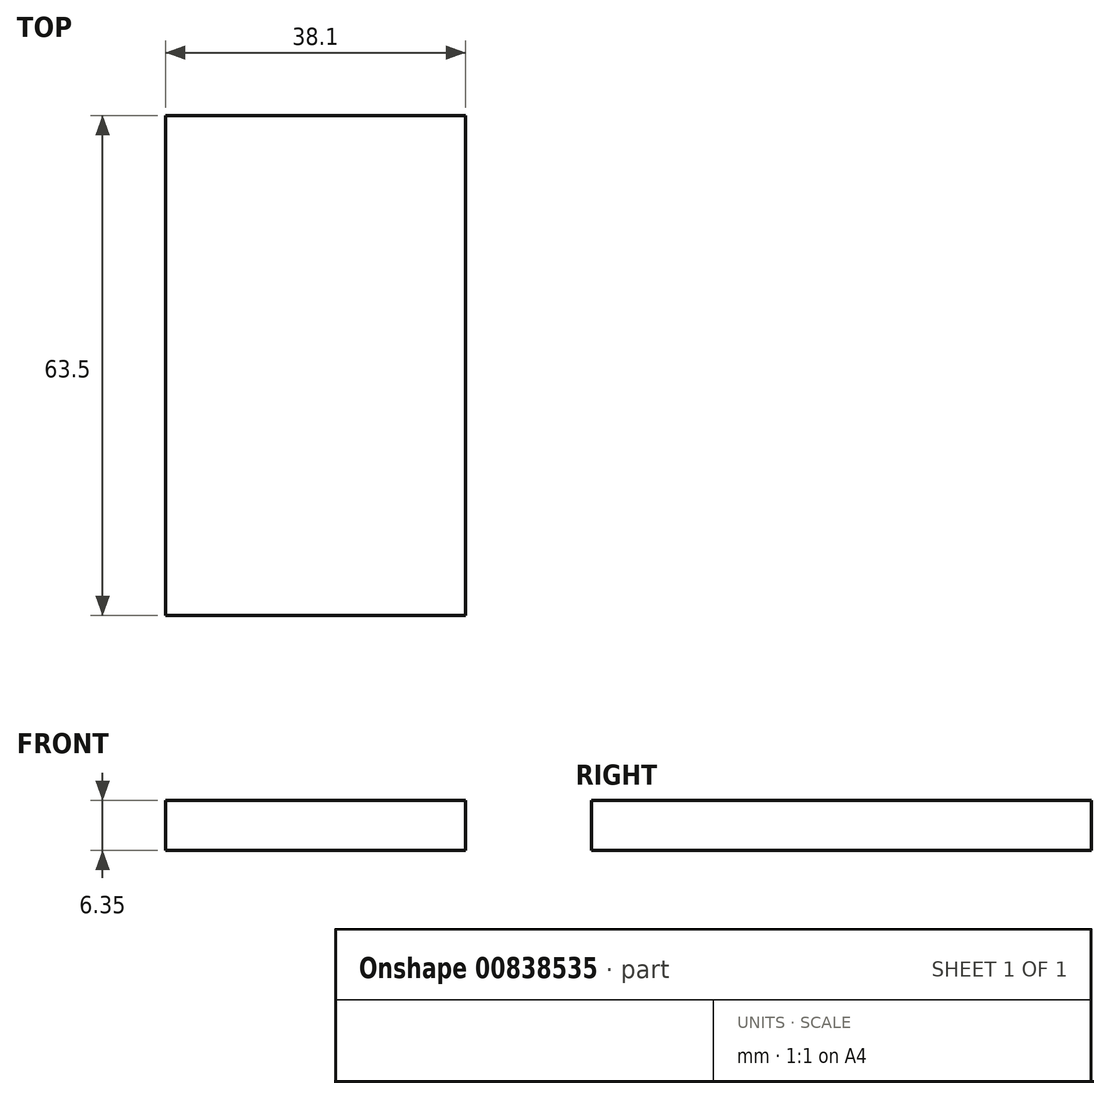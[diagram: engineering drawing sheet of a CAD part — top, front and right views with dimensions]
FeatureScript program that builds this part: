
annotation { "Feature Type Name" : "Feature", "Feature Type Description" : "" }
export const myFeature = defineFeature(function(context is Context, id is Id, definition is map)
    precondition{}
    {
        {
            var Q0;
            Q0=qCreatedBy(makeId("Top.planeOp"),FACE);
            var sketch = newSketch(context, id + "F0", { "sketchPlane" : qUnion([Q0])});
            skLineSegment(sketch, "E0.bottom", {"start": v(-19.85, 35.45) * mm, "end": v(18.25, 35.45) * mm});
            skLineSegment(sketch, "E0.top", {"start": v(-19.85, -28.05) * mm, "end": v(18.25, -28.05) * mm});
            skLineSegment(sketch, "E0.left", {"start": v(-19.85, 35.45) * mm, "end": v(-19.85, -28.05) * mm});
            skLineSegment(sketch, "E0.right", {"start": v(18.25, 35.45) * mm, "end": v(18.25, -28.05) * mm});
            skSolve(sketch);
        }
        {
            var Q0;
            Q0=makeQuery(id+"F0.imprint","IMPRINT",FACE,{"disambiguationData":[TD([[makeQuery(id+"F0.imprint","IMPRINT",EDGE,{"derivedFrom":sQuery(id+"F0.wireOp",EDGE,"E0.bottom")}),-1.0]])]});
            extrude(context, id + "F1", {"entities" : qUnion([Q0]), "depth" : 6.35 * mm, "offsetDistance" : 25.4 * mm});
        }
    });
